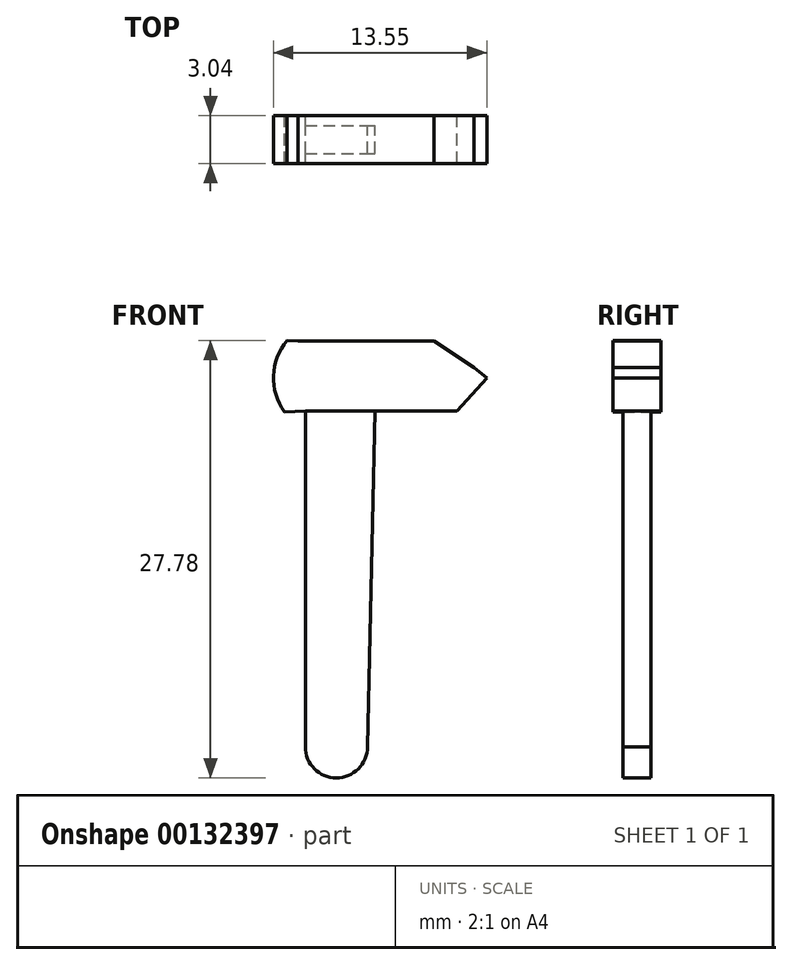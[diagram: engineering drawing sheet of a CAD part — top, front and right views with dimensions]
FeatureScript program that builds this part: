
annotation { "Feature Type Name" : "Feature", "Feature Type Description" : "" }
export const myFeature = defineFeature(function(context is Context, id is Id, definition is map)
    precondition{}
    {
        {
            var Q0;
            Q0=qCreatedBy(makeId("Front.planeOp"),FACE);
            var sketch = newSketch(context, id + "F0", { "sketchPlane" : qUnion([Q0])});
            skLineSegment(sketch, "E0", {"start": v(1.82, -5.95) * mm, "end": v(4.03, -5.95) * mm});
            skLineSegment(sketch, "E1", {"start": v(4.03, -5.95) * mm, "end": v(7, -5.95) * mm});
            skLineSegment(sketch, "E2", {"start": v(-2.12, -1.5) * mm, "end": v(-0.74, -1.5) * mm});
            skLineSegment(sketch, "E3", {"start": v(-0.74, -1.5) * mm, "end": v(2.55, -1.5) * mm});
            skLineSegment(sketch, "E4", {"start": v(-2.62, -5.95) * mm, "end": v(-2.62, -27.28) * mm});
            skLineSegment(sketch, "E5", {"start": v(1.33, -27.28) * mm, "end": v(1.82, -5.95) * mm});
            skArc(sketch, "E6", {"start": v(-3.96, -6) * mm, "mid": v(-4.64, -3.7) * mm, "end": v(-3.8, -1.47) * mm});
            skLineSegment(sketch, "E7", {"start": v(-2.12, -1.5) * mm, "end": v(-3.08, -1.5) * mm});
            skLineSegment(sketch, "E8", {"start": v(-3.08, -1.5) * mm, "end": v(-3.8, -1.47) * mm});
            skLineSegment(sketch, "E9", {"start": v(-2.62, -5.95) * mm, "end": v(-3.96, -6) * mm});
            skLineSegment(sketch, "E10", {"start": v(2.55, -1.5) * mm, "end": v(5.54, -1.5) * mm});
            skLineSegment(sketch, "E11", {"start": v(5.54, -1.5) * mm, "end": v(8.1, -3.17) * mm});
            skLineSegment(sketch, "E12", {"start": v(8.1, -3.17) * mm, "end": v(8.9, -3.84) * mm});
            skLineSegment(sketch, "E13", {"start": v(8.9, -3.84) * mm, "end": v(7, -5.95) * mm});
            skArc(sketch, "E14", {"start": v(-2.62, -27.28) * mm, "mid": v(-0.65, -29.25) * mm, "end": v(1.33, -27.28) * mm});
            skLineSegment(sketch, "E15", {"start": v(-2.62, -5.95) * mm, "end": v(1.82, -5.95) * mm});
            skSolve(sketch);
        }
        {
            var Q0;
            Q0=makeQuery(id+"F0.imprint","IMPRINT",FACE,{"disambiguationData":[TD([[makeQuery(id+"F0.imprint","IMPRINT",EDGE,{"derivedFrom":sQuery(id+"F0.wireOp",EDGE,"E4")}),1.0]])]});
            extrude(context, id + "F1", {"entities" : qUnion([Q0]), "endBound" : BoundingType.SYMMETRIC, "depth" : 1.78 * mm});
        }
        {
            var Q0;
            Q0=makeQuery(id+"F0.imprint","IMPRINT",FACE,{"disambiguationData":[TD([[makeQuery(id+"F0.imprint","IMPRINT",EDGE,{"derivedFrom":sQuery(id+"F0.wireOp",EDGE,"E0")}),1.0]])]});
            extrude(context, id + "F2", {"entities" : qUnion([Q0]), "operationType" : NewBodyOperationType.ADD, "endBound" : BoundingType.SYMMETRIC, "depth" : 3.05 * mm});
        }
    });
